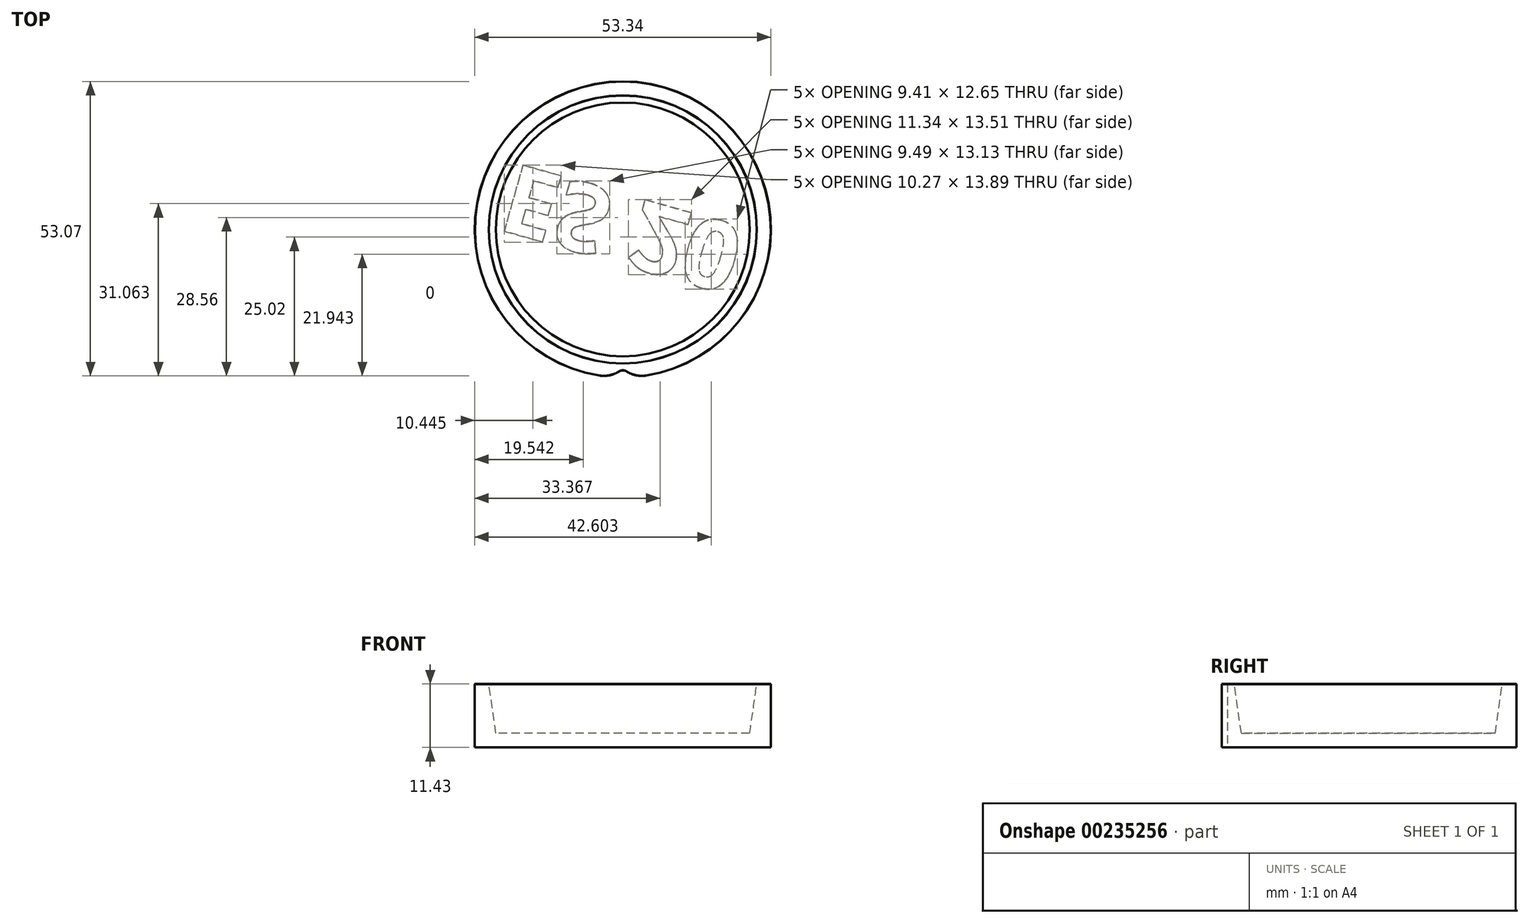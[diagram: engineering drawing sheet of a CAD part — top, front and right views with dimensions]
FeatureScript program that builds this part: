
annotation { "Feature Type Name" : "Feature", "Feature Type Description" : "" }
export const myFeature = defineFeature(function(context is Context, id is Id, definition is map)
    precondition{}
    {
        {
            assignVariable(context, id + "F0", {"name" : "SideThickness", "anyValue" : .1});
        }
        {
            assignVariable(context, id + "F1", {"name" : "TopThickness", "anyValue" : .1});
        }
        {
            var Q0;
            Q0=qCreatedBy(makeId("Front.planeOp"),FACE);
            var sketch = newSketch(context, id + "F2", { "sketchPlane" : qUnion([Q0])});
            skLineSegment(sketch, "E0", {"start": v(0, 0) * mm, "end": v(26.67, 0) * mm});
            skLineSegment(sketch, "E1", {"start": v(26.67, 0) * mm, "end": v(26.67, 11.43) * mm});
            skLineSegment(sketch, "E2", {"start": v(26.67, 11.43) * mm, "end": v(24.13, 11.43) * mm});
            skLineSegment(sketch, "E3", {"start": v(24.13, 11.43) * mm, "end": v(22.86, 2.54) * mm});
            skLineSegment(sketch, "E4", {"start": v(22.86, 2.54) * mm, "end": v(0, 2.54) * mm});
            skLineSegment(sketch, "E5", {"start": v(0, 2.54) * mm, "end": v(0, 0) * mm});
            skLineSegment(sketch, "E6", {"start": v(0, 10.55) * mm, "end": v(0, -12.08) * mm, "construction": true});
            skSolve(sketch);
        }
        {
            var Q0;
            Q0=qSketchRegion(id+"F2",true);
            var Q1;
            Q1=sQuery(id+"F2.wireOp",EDGE,"E6");
            revolve(context, id + "F3", {"surfaceOperationType" : NewSurfaceOperationType.NEW, "entities" : qUnion([Q0]), "axis" : qUnion([Q1]), "revolveType" : RevolveType.FULL});
        }
        {
            var Q0;
            Q0=makeQuery(id+"F3.opRevolve","SWEPT_FACE",FACE,{"disambiguationData":[OSD([sQuery(id+"F2.wireOp",EDGE,"E0")])]});
            var sketch = newSketch(context, id + "F4", { "sketchPlane" : qUnion([Q0])});
            skText(sketch, "E7", { "text": "ES 20 ", "fontName": "OpenSans-Bold.ttf"});
            skCircle(sketch, "E8", {"center": v(0, 0) * mm, "radius": 22.86 * mm, "construction": true});
            const initialGuessF4  = {"E7": [-0.01946, -0.012, 0.96213, 0.27258, 0.01246]};
            skSetInitialGuess(sketch, initialGuessF4);
            skSolve(sketch);
        }
        {
            var Q0;
            Q0=qSketchRegion(id+"F4",true);
            extrude(context, id + "F5", {"entities" : qUnion([Q0]), "operationType" : NewBodyOperationType.REMOVE, "oppositeDirection" : true, "depth" : (getVariable(context, 'TopThickness') / 2) * mm, "offsetDistance" : 25.4 * mm});
        }
        {
            var Q0;
            Q0=makeQuery(id+"F4.imprint","IMPRINT",FACE,{"disambiguationData":[TD([[makeQuery(id+"F4.imprint","IMPRINT",EDGE,{"derivedFrom":sQuery(id+"F4.wireOp",EDGE,"E7.sketch_text.stroke-0")}),1.0]])]});
            var sketch = newSketch(context, id + "F6", { "sketchPlane" : qUnion([Q0])});
            skArc(sketch, "E9", {"start": v(-0.68, 25.6) * mm, "mid": v(0, 25.4) * mm, "end": v(0.68, 25.6) * mm});
            skPoint(sketch, "E10.visualSharp", {"position": v(-1.27, 26.64) * mm});
            skArc(sketch, "E10.filletArc", {"start": v(-0.68, 25.6) * mm, "mid": v(-2.38, 26.3) * mm, "end": v(-4.22, 26.33) * mm});
            skPoint(sketch, "E11.visualSharp", {"position": v(1.27, 26.64) * mm});
            skArc(sketch, "E11.filletArc", {"start": v(4.22, 26.33) * mm, "mid": v(2.38, 26.3) * mm, "end": v(0.68, 25.6) * mm});
            skArc(sketch, "E12", {"start": v(4.22, 26.33) * mm, "mid": v(0, 26.67) * mm, "end": v(-4.22, 26.33) * mm});
            skSolve(sketch);
        }
        {
            var Q0;
            Q0=qSketchRegion(id+"F6",true);
            extrude(context, id + "F7", {"entities" : qUnion([Q0]), "operationType" : NewBodyOperationType.REMOVE, "endBound" : BoundingType.THROUGH_ALL, "oppositeDirection" : true, "depth" : 25.4 * mm, "offsetDistance" : 25.4 * mm});
        }
        {
            var Q0;
            Q0=makeQuery(id+"F5.boolean.opBoolean","SPLIT",FACE,{"disambiguationData":[TD([makeQuery(id+"F3.opRevolve","SWEPT_FACE",FACE,{"disambiguationData":[OSD([sQuery(id+"F2.wireOp",EDGE,"E1")])]})])],"derivedFrom":makeQuery(id+"F3.opRevolve","SWEPT_FACE",FACE,{"disambiguationData":[OSD([sQuery(id+"F2.wireOp",EDGE,"E0")])]})});
            chamfer(context, id + "F8", {"entities" : qUnion([Q0]), "width" : (getVariable(context, 'SideThickness') / 4) * mm, "tangentPropagation" : true});
        }
        {
            var Q0;
            Q0=makeQuery(id+"F3.opRevolve","SWEPT_FACE",FACE,{"disambiguationData":[OSD([sQuery(id+"F2.wireOp",EDGE,"E2")])]});
            chamfer(context, id + "F9", {"entities" : qUnion([Q0]), "width" : (getVariable(context, 'SideThickness') / 4) * mm, "tangentPropagation" : true});
        }
    });
